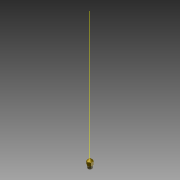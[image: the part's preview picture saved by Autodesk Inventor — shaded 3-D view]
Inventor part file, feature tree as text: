
AUTODESK INVENTOR PART (.ipt)
format: ipt  version: 2015 (Build 190159000, 159)  size: 119,296 bytes
history: native  units: mm
features: extrude x2, imported_body x1, thread x1
ambient origin geometry x8: Origin, YZ Plane, XZ Plane, XY Plane, X Axis, Y Axis, Z Axis, Center Point
bodies: Solid1 (feature_tree)
feature tree (4):
  imported_body  "Base1"
  thread  "Rosca1"  [1 undecoded]
  extrude  "Extrusión1"  Depth=5.0mm
  extrude  "Extrusión2"  Depth=0.75mm TaperAngle=0.0deg
note: 1 required parameter value undecoded (feature->parameter linkage not recoverable at this tier; creation-order binding heuristic only, values carry confidence <= 0.55)
